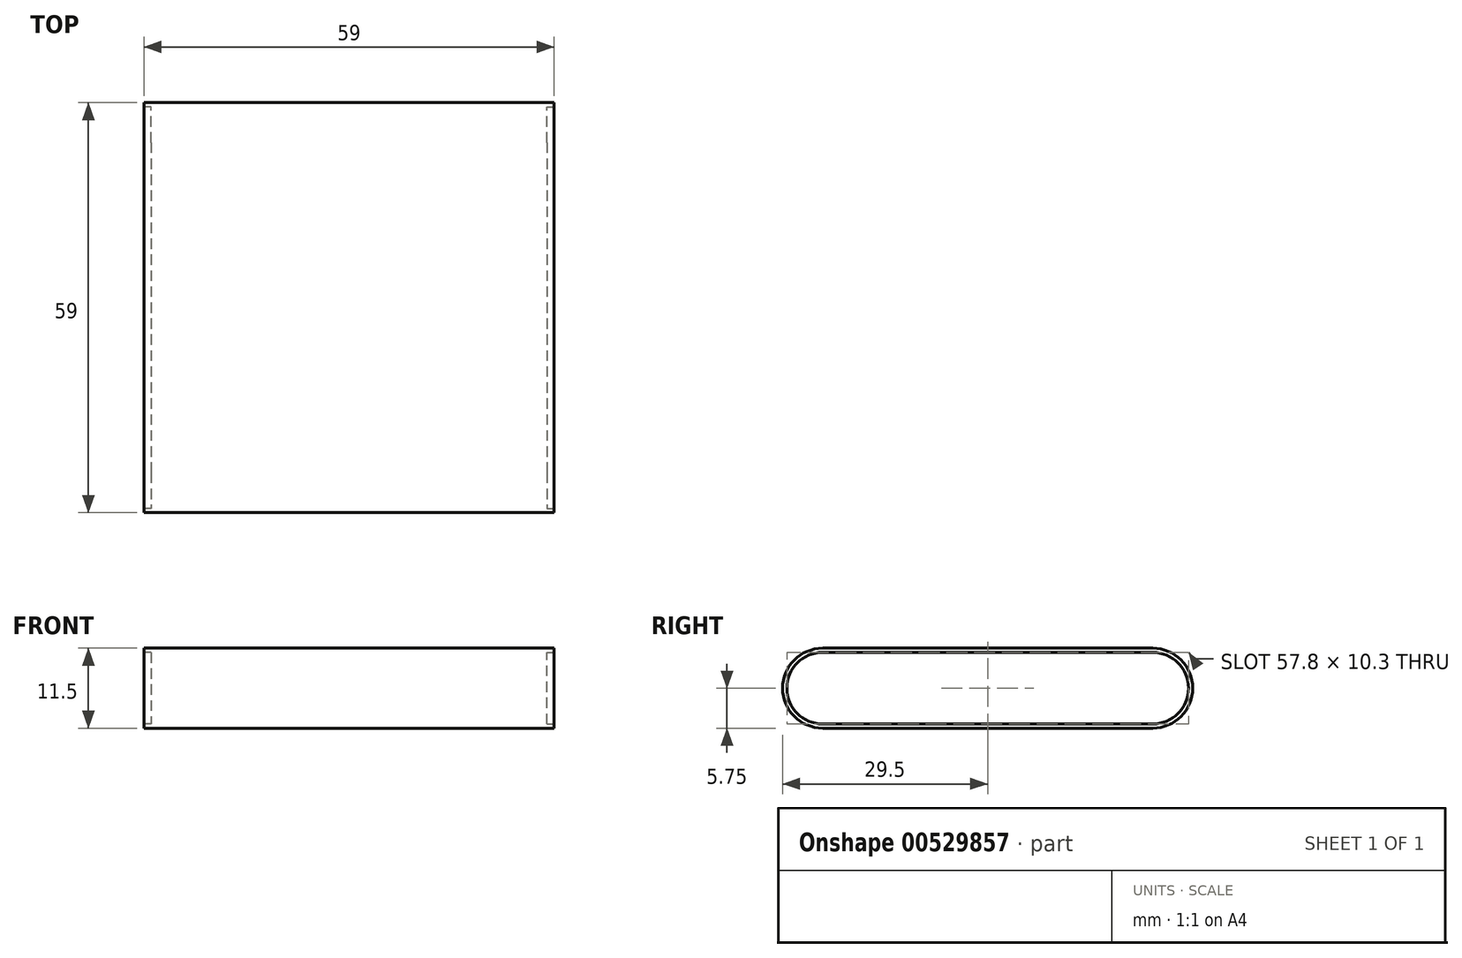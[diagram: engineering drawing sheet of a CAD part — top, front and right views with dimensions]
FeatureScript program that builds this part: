
annotation { "Feature Type Name" : "Feature", "Feature Type Description" : "" }
export const myFeature = defineFeature(function(context is Context, id is Id, definition is map)
    precondition{}
    {
        {
            var Q0;
            Q0=qCreatedBy(makeId("Top.planeOp"),FACE);
            var sketch = newSketch(context, id + "F0", { "sketchPlane" : qUnion([Q0])});
            skLineSegment(sketch, "E0.bottom", {"start": v(0, 0) * mm, "end": v(59, 0) * mm});
            skLineSegment(sketch, "E0.top", {"start": v(0, -59) * mm, "end": v(59, -59) * mm});
            skLineSegment(sketch, "E0.left", {"start": v(0, 0) * mm, "end": v(0, -59) * mm});
            skLineSegment(sketch, "E0.right", {"start": v(59, 0) * mm, "end": v(59, -59) * mm});
            skSolve(sketch);
        }
        {
            var Q0;
            Q0 = qSketchRegion(id + "F0", true);
            extrude(context, id + "F1", {"entities" : qUnion([Q0]), "depth" : 11.5 * mm, "offsetDistance" : 25 * mm});
        }
        {
            var Q0;
            Q0=makeQuery(id+"F1.opExtrude","CAP_EDGE",EDGE,{"disambiguationData":[OSD([sQuery(id+"F0.wireOp",EDGE,"E0.top")])],"isStart":false});
            var Q1;
            Q1=makeQuery(id+"F1.opExtrude","CAP_EDGE",EDGE,{"disambiguationData":[OSD([sQuery(id+"F0.wireOp",EDGE,"E0.top")])],"isStart":true});
            var Q2;
            Q2=makeQuery(id+"F1.opExtrude","CAP_EDGE",EDGE,{"disambiguationData":[OSD([sQuery(id+"F0.wireOp",EDGE,"E0.bottom")])],"isStart":false});
            var Q3;
            Q3=makeQuery(id+"F1.opExtrude","CAP_EDGE",EDGE,{"disambiguationData":[OSD([sQuery(id+"F0.wireOp",EDGE,"E0.bottom")])],"isStart":true});
            fillet(context, id + "F2", {"entities" : qUnion([Q0, Q1, Q2, Q3]), "radius" : 5.75 * mm, "tangentPropagation" : true, "allowEdgeOverflow" : false});
        }
        {
            var Q0;
            Q0=makeQuery(id+"F1.opExtrude","SWEPT_FACE",FACE,{"disambiguationData":[OSD([sQuery(id+"F0.wireOp",EDGE,"E0.right")])]});
            var sketch = newSketch(context, id + "F3", { "sketchPlane" : qUnion([Q0])});
            skLineSegment(sketch, "E1.0", {"start": v(-5.75, 10.9) * mm, "end": v(-53.25, 10.9) * mm});
            skArc(sketch, "E1.1", {"start": v(-5.75, 0.6) * mm, "mid": v(-0.6, 5.75) * mm, "end": v(-5.75, 10.9) * mm});
            skLineSegment(sketch, "E1.2", {"start": v(-5.75, 0.6) * mm, "end": v(-53.25, 0.6) * mm});
            skArc(sketch, "E1.3", {"start": v(-53.25, 10.9) * mm, "mid": v(-58.4, 5.75) * mm, "end": v(-53.25, 0.6) * mm});
            skSolve(sketch);
        }
        {
            var Q0;
            Q0 = qSketchRegion(id + "F3", true);
            extrude(context, id + "F4", {"entities" : qUnion([Q0]), "operationType" : NewBodyOperationType.REMOVE, "oppositeDirection" : true, "depth" : 1 * mm, "offsetDistance" : 25 * mm});
        }
        {
            var Q0;
            Q0=makeQuery(id+"F1.opExtrude","SWEPT_FACE",FACE,{"disambiguationData":[OSD([sQuery(id+"F0.wireOp",EDGE,"E0.left")])]});
            var sketch = newSketch(context, id + "F5", { "sketchPlane" : qUnion([Q0])});
            skLineSegment(sketch, "E2.0", {"start": v(5.75, 10.9) * mm, "end": v(53.25, 10.9) * mm});
            skArc(sketch, "E2.1", {"start": v(5.75, 10.9) * mm, "mid": v(0.6, 5.75) * mm, "end": v(5.75, 0.6) * mm});
            skLineSegment(sketch, "E2.2", {"start": v(5.75, 0.6) * mm, "end": v(53.25, 0.6) * mm});
            skArc(sketch, "E2.3", {"start": v(53.25, 0.6) * mm, "mid": v(58.4, 5.75) * mm, "end": v(53.25, 10.9) * mm});
            skSolve(sketch);
        }
        {
            var Q0;
            Q0 = qSketchRegion(id + "F5", true);
            extrude(context, id + "F6", {"entities" : qUnion([Q0]), "operationType" : NewBodyOperationType.REMOVE, "oppositeDirection" : true, "depth" : 1 * mm, "offsetDistance" : 25 * mm});
        }
    });
